# Revit family: 06-30-029-DN700-1000
name_source: partatom
category: Pipe Accessories
units: mm (PartAtom-declared; Revit-internal decimal feet)

## family parameters
Always vertical = No
Cut with Voids When Loaded = No
OmniClass Number = 23.60.00.00
OmniClass Title = General Purpose: Services
Part Type = Valve - Breaks Into
Round Connector Dimension = Use Diameter
Shared = Yes
Work Plane-Based = No

## types (8) — shared parameters
Bonnet_Flange_cut = 35 mm  [stored 0.114829 ft]
Bonnet_Flange_thickness = 70 mm  [stored 0.229659 ft]
D2 = 20 mm  [stored 0.0656168 ft]
DN 1000 = Yes
DN 700 = Yes
DN 800 = Yes
DN 900 = Yes
DN1000_PN10 = 06-1000-30-09043164
DN1000_PN16 = 06-1000-30-09143164
DN700_PN10 = 06-700-30-00464
DN700_PN16 = 06-700-30-01464
DN800_PN10 = 06-800-30-00464
DN800_PN16 = 06-800-30-01464
DN900_PN10 = 06-900-30-00464
DN900_PN16 = 06-900-30-01464
Description_ = AVK_GATE_VALVE,FLANGED
F2 = 81 mm  [stored 0.265748 ft]
Fillet_Thickness = 32 mm  [stored 0.104987 ft]
Ftc = 4 mm  [stored 0.0131234 ft]
Gearbox_Flange_Dia = 87.5 mm  [stored 0.287073 ft]
Gearbox_Flangethickness = 10 mm  [stored 0.0328084 ft]
Name_Height_reference = 10 mm  [stored 0.0328084 ft]
R2f = 80 mm  [stored 0.262467 ft]
Rib_Thickness = 18 mm  [stored 0.0590551 ft]
Search_table = 06-30-029-DN700-1000
Tf = 26 mm
URL product pages = https://www.avkvalves.com
zero-valued in all types: Bottom_Reference

## per-type parameters (varying)
- DN 700-PN10: At=535 mm; Body_Height=780 mm; Body_Wallthickness=365.05 mm; Body_depth=1070 mm; Body_width=180 mm  [stored 0.590551 ft]; Bonnet_Flange_Depth=1192 mm; Bonnet_Flange_Width=266 mm; Bonnet_Height=227.5 mm; Bonnet_Reference_height=770 mm; Bonnet_Thickness=183.6 mm  [stored 0.602362 ft]; Bt=183.6 mm  [stored 0.602362 ft]; Bt_2=174 mm  [stored 0.570866 ft]; CL=751 mm; CL _Thickness=34.33 mm; CL_2=721 mm; CL_Thickness 2=58.67 mm; Cut_Reference=860 mm; Flange_OR=455 mm; Flange_Thickness=28 mm  [stored 0.0918635 ft]; Flange_Thickness_cut=52.48 mm; Ftc_reference_height=455 mm; H=1622 mm; H3=2070 mm; Horizontal_Flange_width=896 mm; ID (Radius)=350.05 mm; L=430 mm; L_Dia=700.1 mm; Name_Reference=475 mm; Name_Width=90 mm  [stored 0.295276 ft]; Nominal Diameter (DN)=700.1 mm; R1tv=4550 mm; RF_Dia=397 mm; Rf=1493.33 mm; Rib_Height_Reference_1=150 mm  [stored 0.492126 ft]; Rib_Height_Reference_2=340 mm; Rib_Height_Reference_3=492 mm; Rib_Height_Reference_4=650 mm; Rib_Width_1=160 mm  [stored 0.524934 ft]; Rib_Width_2=160 mm  [stored 0.524934 ft]; Rib_Width_3=160 mm  [stored 0.524934 ft]; Rib_depth_1=1211 mm; Rib_depth_2=1211 mm; Rib_depth_3=1211 mm; Rt=1516.67 mm; W=1211 mm
- DN 700-PN16: At=535 mm; Body_Height=780 mm; Body_Wallthickness=365.08 mm; Body_depth=1070 mm; Body_width=180 mm  [stored 0.590551 ft]; Bonnet_Flange_Depth=1192 mm; Bonnet_Flange_Width=266 mm; Bonnet_Height=227.5 mm; Bonnet_Reference_height=770 mm; Bonnet_Thickness=183.6 mm  [stored 0.602362 ft]; Bt=183.6 mm  [stored 0.602362 ft]; Bt_2=174 mm  [stored 0.570866 ft]; CL=751 mm; CL _Thickness=34.33 mm; CL_2=721 mm; CL_Thickness 2=58.67 mm; Cut_Reference=860 mm; Flange_OR=455 mm; Flange_Thickness=28 mm  [stored 0.0918635 ft]; Flange_Thickness_cut=52.46 mm; Ftc_reference_height=455 mm; H=1622 mm; H3=2077 mm; Horizontal_Flange_width=910 mm; ID (Radius)=350.08 mm; L=430 mm; L_Dia=700.16 mm; Name_Reference=475 mm; Name_Width=90 mm  [stored 0.295276 ft]; Nominal Diameter (DN)=700.16 mm; R1tv=4550 mm; RF_Dia=397 mm; Rf=1516.67 mm; Rib_Height_Reference_1=150 mm  [stored 0.492126 ft]; Rib_Height_Reference_2=340 mm; Rib_Height_Reference_3=492 mm; Rib_Height_Reference_4=650 mm; Rib_Width_1=160 mm  [stored 0.524934 ft]; Rib_Width_2=160 mm  [stored 0.524934 ft]; Rib_Width_3=160 mm  [stored 0.524934 ft]; Rib_depth_1=1211 mm; Rib_depth_2=1211 mm; Rib_depth_3=1211 mm; Rt=1516.67 mm; W=1211 mm
- DN 800-PN10: At=548.5 mm; Body_Height=830 mm; Body_Wallthickness=415.05 mm; Body_depth=1097 mm; Body_width=210 mm; Bonnet_Flange_Depth=1515 mm; Bonnet_Flange_Width=266 mm; Bonnet_Height=256.25 mm; Bonnet_Reference_height=820 mm; Bonnet_Thickness=214.2 mm; Bt=214.2 mm; Bt_2=204 mm; CL=751 mm; CL _Thickness=34.33 mm; CL_2=721 mm; CL_Thickness 2=58.67 mm; Cut_Reference=940 mm; Flange_OR=512.5 mm; Flange_Thickness=30 mm  [stored 0.0984252 ft]; Flange_Thickness_cut=56.23 mm; Ftc_reference_height=512.5 mm; H=1672 mm; H3=2180 mm; Horizontal_Flange_width=1016 mm; ID (Radius)=400.05 mm; L=470 mm; L_Dia=800.1 mm; Name_Reference=665 mm; Name_Width=105 mm  [stored 0.344488 ft]; Nominal Diameter (DN)=800.1 mm; R1tv=5125 mm; RF_Dia=450.2 mm; Rf=1693.33 mm; Rib_Height_Reference_1=200 mm; Rib_Height_Reference_2=350 mm; Rib_Height_Reference_3=550 mm; Rib_Height_Reference_4=750 mm; Rib_Width_1=160 mm  [stored 0.524934 ft]; Rib_Width_2=160 mm  [stored 0.524934 ft]; Rib_Width_3=160 mm  [stored 0.524934 ft]; Rib_depth_1=1211 mm; Rib_depth_2=1211 mm; Rib_depth_3=1211 mm; Rt=1708.33 mm; W=1211 mm
- DN 900-PN10: At=678 mm; Body_Height=1088 mm; Body_Wallthickness=465.05 mm; Body_depth=1356 mm; Body_width=190 mm; Bonnet_Flange_Depth=1515 mm; Bonnet_Flange_Width=339 mm; Bonnet_Height=278.75 mm; Bonnet_Reference_height=1078 mm; Bonnet_Thickness=193.8 mm; Bt=193.8 mm; Bt_2=184 mm; CL=938 mm; CL _Thickness=46.5 mm  [stored 0.152559 ft]; CL_2=908 mm; CL_Thickness 2=83 mm  [stored 0.27231 ft]; Cut_Reference=1020 mm; Flange_OR=557.5 mm; Flange_Thickness=31.5 mm  [stored 0.103346 ft]; Flange_Thickness_cut=53.73 mm; Ftc_reference_height=557.5 mm; H=2117 mm; H3=2675 mm; Horizontal_Flange_width=1116 mm; ID (Radius)=450.05 mm; L=510 mm; L_Dia=900.1 mm; Name_Reference=590 mm; Name_Width=95 mm; Nominal Diameter (DN)=900.1 mm; R1tv=5575 mm; RF_Dia=500.5 mm; Rf=1860 mm; Rib_Height_Reference_1=250 mm; Rib_Height_Reference_2=400 mm; Rib_Height_Reference_3=690 mm; Rib_Height_Reference_4=900 mm; Rib_Width_1=100 mm  [stored 0.328084 ft]; Rib_Width_2=100 mm  [stored 0.328084 ft]; Rib_Width_3=100 mm  [stored 0.328084 ft]; Rib_depth_1=1523 mm; Rib_depth_2=1523 mm; Rib_depth_3=1523 mm; Rt=1858.33 mm; W=1523 mm
- DN 800-PN16: At=548.5 mm; Body_Height=830 mm; Body_Wallthickness=415.08 mm; Body_depth=1097 mm; Body_width=210 mm; Bonnet_Flange_Depth=1515 mm; Bonnet_Flange_Width=266 mm; Bonnet_Height=256.25 mm; Bonnet_Reference_height=820 mm; Bonnet_Thickness=214.2 mm; Bt=214.2 mm; Bt_2=204 mm; CL=751 mm; CL _Thickness=34.33 mm; CL_2=721 mm; CL_Thickness 2=58.67 mm; Cut_Reference=940 mm; Flange_OR=512.5 mm; Flange_Thickness=30 mm  [stored 0.0984252 ft]; Flange_Thickness_cut=56.21 mm; Ftc_reference_height=512.5 mm; H=1672 mm; H3=2185 mm; Horizontal_Flange_width=1026 mm; ID (Radius)=400.08 mm; L=470 mm; L_Dia=800.16 mm; Name_Reference=665 mm; Name_Width=105 mm  [stored 0.344488 ft]; Nominal Diameter (DN)=800.16 mm; R1tv=5125 mm; RF_Dia=450.2 mm; Rf=1710 mm; Rib_Height_Reference_1=200 mm; Rib_Height_Reference_2=350 mm; Rib_Height_Reference_3=550 mm; Rib_Height_Reference_4=750 mm; Rib_Width_1=160 mm  [stored 0.524934 ft]; Rib_Width_2=160 mm  [stored 0.524934 ft]; Rib_Width_3=160 mm  [stored 0.524934 ft]; Rib_depth_1=1211 mm; Rib_depth_2=1211 mm; Rib_depth_3=1211 mm; Rt=1708.33 mm; W=1211 mm
- DN 900-PN16: At=678 mm; Body_Height=1088 mm; Body_Wallthickness=465.08 mm; Body_depth=1356 mm; Body_width=190 mm; Bonnet_Flange_Depth=1515 mm; Bonnet_Flange_Width=339 mm; Bonnet_Height=281.25 mm; Bonnet_Reference_height=1078 mm; Bonnet_Thickness=193.8 mm; Bt=193.8 mm; Bt_2=184 mm; CL=938 mm; CL _Thickness=46.5 mm  [stored 0.152559 ft]; CL_2=908 mm; CL_Thickness 2=83 mm  [stored 0.27231 ft]; Cut_Reference=1020 mm; Flange_OR=562.5 mm; Flange_Thickness=31.5 mm  [stored 0.103346 ft]; Flange_Thickness_cut=56.21 mm; Ftc_reference_height=562.5 mm; H=2117 mm; H3=2680 mm; Horizontal_Flange_width=1126 mm; ID (Radius)=450.08 mm; L=510 mm; L_Dia=900.16 mm; Name_Reference=590 mm; Name_Width=95 mm; Nominal Diameter (DN)=900.16 mm; R1tv=5625 mm; RF_Dia=500.5 mm; Rf=1876.67 mm; Rib_Height_Reference_1=250 mm; Rib_Height_Reference_2=400 mm; Rib_Height_Reference_3=690 mm; Rib_Height_Reference_4=900 mm; Rib_Width_1=100 mm  [stored 0.328084 ft]; Rib_Width_2=100 mm  [stored 0.328084 ft]; Rib_Width_3=100 mm  [stored 0.328084 ft]; Rib_depth_1=1523 mm; Rib_depth_2=1523 mm; Rib_depth_3=1523 mm; Rt=1875 mm; W=1523 mm
- DN 1000-PN16: At=670 mm; Body_Height=1038 mm; Body_Wallthickness=515.08 mm; Body_depth=1340 mm; Body_width=250 mm; Bonnet_Flange_Depth=1515 mm; Bonnet_Flange_Width=339 mm; Bonnet_Height=313.75 mm; Bonnet_Reference_height=1028 mm; Bonnet_Thickness=255 mm; Bt=255 mm; Bt_2=244 mm; CL=938 mm; CL _Thickness=46.5 mm  [stored 0.152559 ft]; CL_2=908 mm; CL_Thickness 2=83 mm  [stored 0.27231 ft]; Cut_Reference=1100 mm; Flange_OR=627.5 mm; Flange_Thickness=36 mm  [stored 0.11811 ft]; Flange_Thickness_cut=63.71 mm; Ftc_reference_height=627.5 mm; H=2067 mm; H3=2695 mm; Horizontal_Flange_width=1256 mm; ID (Radius)=500.08 mm; L=550 mm; L_Dia=1000.16 mm; Name_Reference=655 mm; Name_Width=125 mm  [stored 0.410105 ft]; Nominal Diameter (DN)=1000.16 mm; R1tv=6275 mm; RF_Dia=556 mm; Rf=2093.33 mm; Rib_Height_Reference_1=300 mm; Rib_Height_Reference_2=490 mm; Rib_Height_Reference_3=725 mm; Rib_Height_Reference_4=900 mm; Rib_Width_1=145 mm  [stored 0.475722 ft]; Rib_Width_2=145 mm  [stored 0.475722 ft]; Rib_Width_3=145 mm  [stored 0.475722 ft]; Rib_depth_1=1563 mm; Rib_depth_2=1563 mm; Rib_depth_3=1563 mm; Rt=2091.67 mm; W=1563 mm
- DN 1000-PN10: At=670 mm; Body_Height=1038 mm; Body_Wallthickness=515.05 mm; Body_depth=1340 mm; Body_width=250 mm; Bonnet_Flange_Depth=1515 mm; Bonnet_Flange_Width=339 mm; Bonnet_Height=307.5 mm; Bonnet_Reference_height=1028 mm; Bonnet_Thickness=255 mm; Bt=255 mm; Bt_2=244 mm; CL=938 mm; CL _Thickness=46.5 mm  [stored 0.152559 ft]; CL_2=908 mm; CL_Thickness 2=83 mm  [stored 0.27231 ft]; Cut_Reference=1100 mm; Flange_OR=615 mm; Flange_Thickness=36 mm  [stored 0.11811 ft]; Flange_Thickness_cut=57.48 mm; Ftc_reference_height=615 mm; H=2067 mm; H3=2682 mm; Horizontal_Flange_width=1230 mm; ID (Radius)=500.05 mm; L=550 mm; L_Dia=1000.1 mm; Name_Reference=655 mm; Name_Width=125 mm  [stored 0.410105 ft]; Nominal Diameter (DN)=1000.1 mm; R1tv=6150 mm; RF_Dia=556 mm; Rf=2050 mm; Rib_Height_Reference_1=300 mm; Rib_Height_Reference_2=490 mm; Rib_Height_Reference_3=725 mm; Rib_Height_Reference_4=900 mm; Rib_Width_1=140 mm  [stored 0.459318 ft]; Rib_Width_2=140 mm  [stored 0.459318 ft]; Rib_Width_3=140 mm  [stored 0.459318 ft]; Rib_depth_1=1563 mm; Rib_depth_2=1563 mm; Rib_depth_3=1563 mm; Rt=2050 mm; W=1563 mm

note: [stored X ft] marks values corroborated as IEEE doubles in the binary element streams (Revit-internal decimal feet)

## geometry (parser evidence)
native form markers: Extrusion x1, Sweep x4
no freeform markers — native parametric forms only
